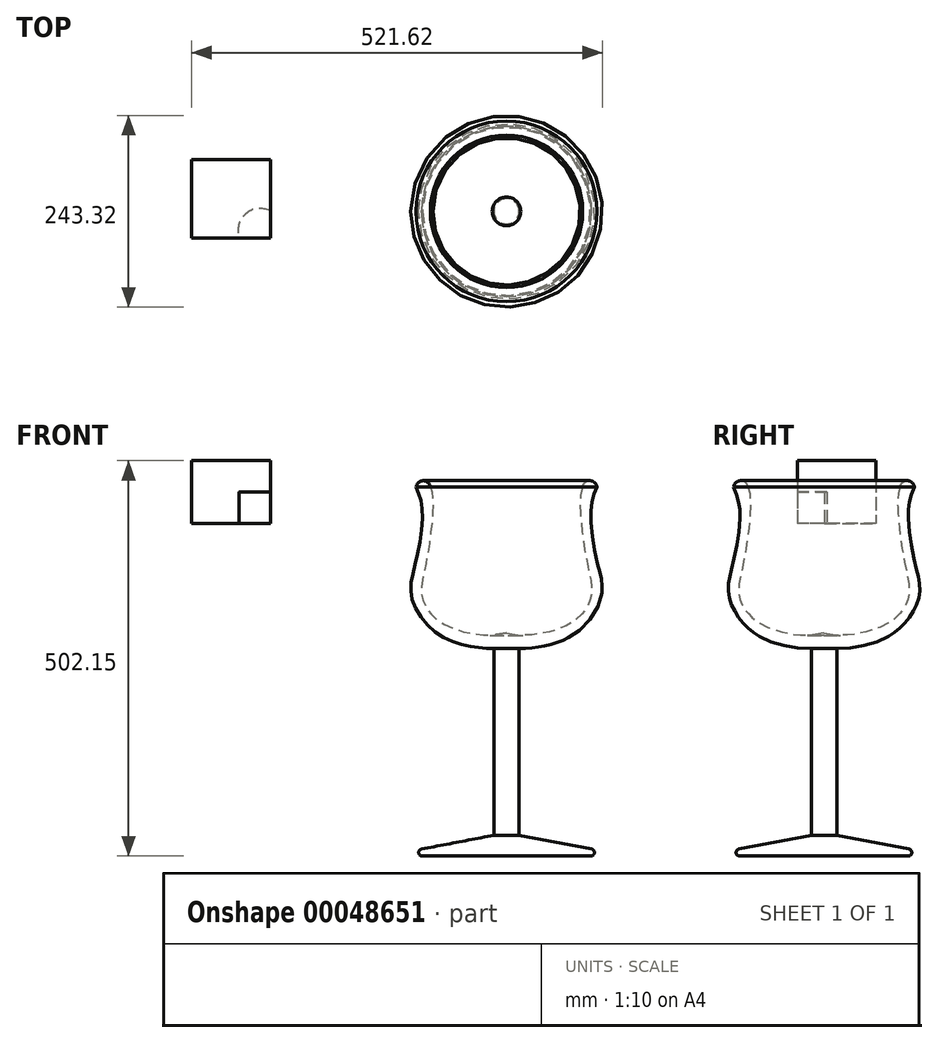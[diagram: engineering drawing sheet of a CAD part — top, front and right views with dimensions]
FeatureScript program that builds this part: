
annotation { "Feature Type Name" : "Feature", "Feature Type Description" : "" }
export const myFeature = defineFeature(function(context is Context, id is Id, definition is map)
    precondition{}
    {
        {
            assignVariable(context, id + "F0", {"name" : "teste", "anyValue" : 80});
        }
        {
            var Q0;
            Q0=qCreatedBy(makeId("Top.planeOp"),FACE);
            var sketch = newSketch(context, id + "F1", { "sketchPlane" : qUnion([Q0])});
            skLineSegment(sketch, "E0", {"start": v(-47.92, 65.98) * mm, "end": v(-47.92, -34.02) * mm});
            skLineSegment(sketch, "E1", {"start": v(-47.92, -34.02) * mm, "end": v(52.08, -34.02) * mm});
            skLineSegment(sketch, "E2", {"start": v(52.08, -34.02) * mm, "end": v(52.08, 65.98) * mm});
            skLineSegment(sketch, "E3", {"start": v(52.08, 65.98) * mm, "end": v(-47.92, 65.98) * mm});
            skSolve(sketch);
        }
        {
            var Q0;
            Q0=makeQuery(id+"F1.imprint","IMPRINT",FACE,{"disambiguationData":[TD([[makeQuery(id+"F1.imprint","IMPRINT",EDGE,{"derivedFrom":sQuery(id+"F1.wireOp",EDGE,"E0")}),1.0]])]});
            extrude(context, id + "F2", {"entities" : qUnion([Q0]), "depth" : (getVariable(context, 'teste')) * mm});
        }
        {
            var Q0;
            Q0=qCreatedBy(makeId("Top.planeOp"),FACE);
            var sketch = newSketch(context, id + "F3", { "sketchPlane" : qUnion([Q0])});
            skCircle(sketch, "E4", {"center": v(39.16, -24.62) * mm, "radius": 28.25 * mm});
            skSolve(sketch);
        }
        {
            var Q0;
            Q0=makeQuery(id+"F3.imprint","IMPRINT",FACE,{"disambiguationData":[TD([[makeQuery(id+"F3.imprint","IMPRINT",EDGE,{"derivedFrom":sQuery(id+"F3.wireOp",EDGE,"E4")}),1.0]])]});
            var Q1;
            Q1=sQuery(id+"F3.wireOp",EDGE,"E4");
            extrude(context, id + "F4", {"entities" : qUnion([Q0]), "operationType" : NewBodyOperationType.REMOVE, "surfaceEntities" : qUnion([Q1]), "depth" : (getVariable(context, 'teste') / 2) * mm});
        }
        {
            var Q0;
            Q0=qCreatedBy(makeId("Front.planeOp"),FACE);
            var sketch = newSketch(context, id + "F5", { "sketchPlane" : qUnion([Q0])});
            skFitSpline(sketch, "E5", {"points": [v(237.23, 46.56) * mm, v(245, 17.22) * mm, v(236.34, -50.95) * mm, v(231.14, -91.5) * mm, v(257.9, -134.64) * mm, v(302.8, -155.35) * mm, v(335.91, -158.8) * mm], "startDerivative": vector(76.12, -182.84) * mm, "endDerivative": vector(218.8, -9.6) * mm});
            skLineSegment(sketch, "E6", {"start": v(335.91, -158.8) * mm, "end": v(335.91, -396.03) * mm});
            skLineSegment(sketch, "E7", {"start": v(335.91, -396.03) * mm, "end": v(244.01, -413.46) * mm});
            skArc(sketch, "E8", {"start": v(244.01, -413.46) * mm, "mid": v(240.42, -417.8) * mm, "end": v(244.01, -422.15) * mm});
            skLineSegment(sketch, "E9", {"start": v(244.01, -422.15) * mm, "end": v(352.05, -422.15) * mm});
            skLineSegment(sketch, "E10", {"start": v(352.05, -422.15) * mm, "end": v(352.05, -139.08) * mm});
            skArc(sketch, "E11", {"start": v(255.31, 46.53) * mm, "mid": v(246.29, 54.56) * mm, "end": v(237.23, 46.56) * mm});
            skLineSegment(sketch, "E12", {"start": v(333.92, -141.84) * mm, "end": v(352.05, -139.08) * mm});
            skFitSpline(sketch, "E13", {"points": [v(255.31, 46.53) * mm, v(258.47, 20.04) * mm, v(249.45, -51.03) * mm, v(244.3, -91.18) * mm, v(269.26, -125.88) * mm, v(333.92, -141.84) * mm], "startDerivative": vector(56.85, -142.23) * mm, "endDerivative": vector(242.6, 6.94) * mm});
            skSolve(sketch);
        }
        {
            var Q0;
            Q0 = qSketchRegion(id + "F5", true);
            var Q1;
            Q1=sQuery(id+"F5.wireOp",EDGE,"E10");
            revolve(context, id + "F6", {"entities" : qUnion([Q0]), "axis" : qUnion([Q1]), "revolveType" : RevolveType.FULL});
        }
    });
